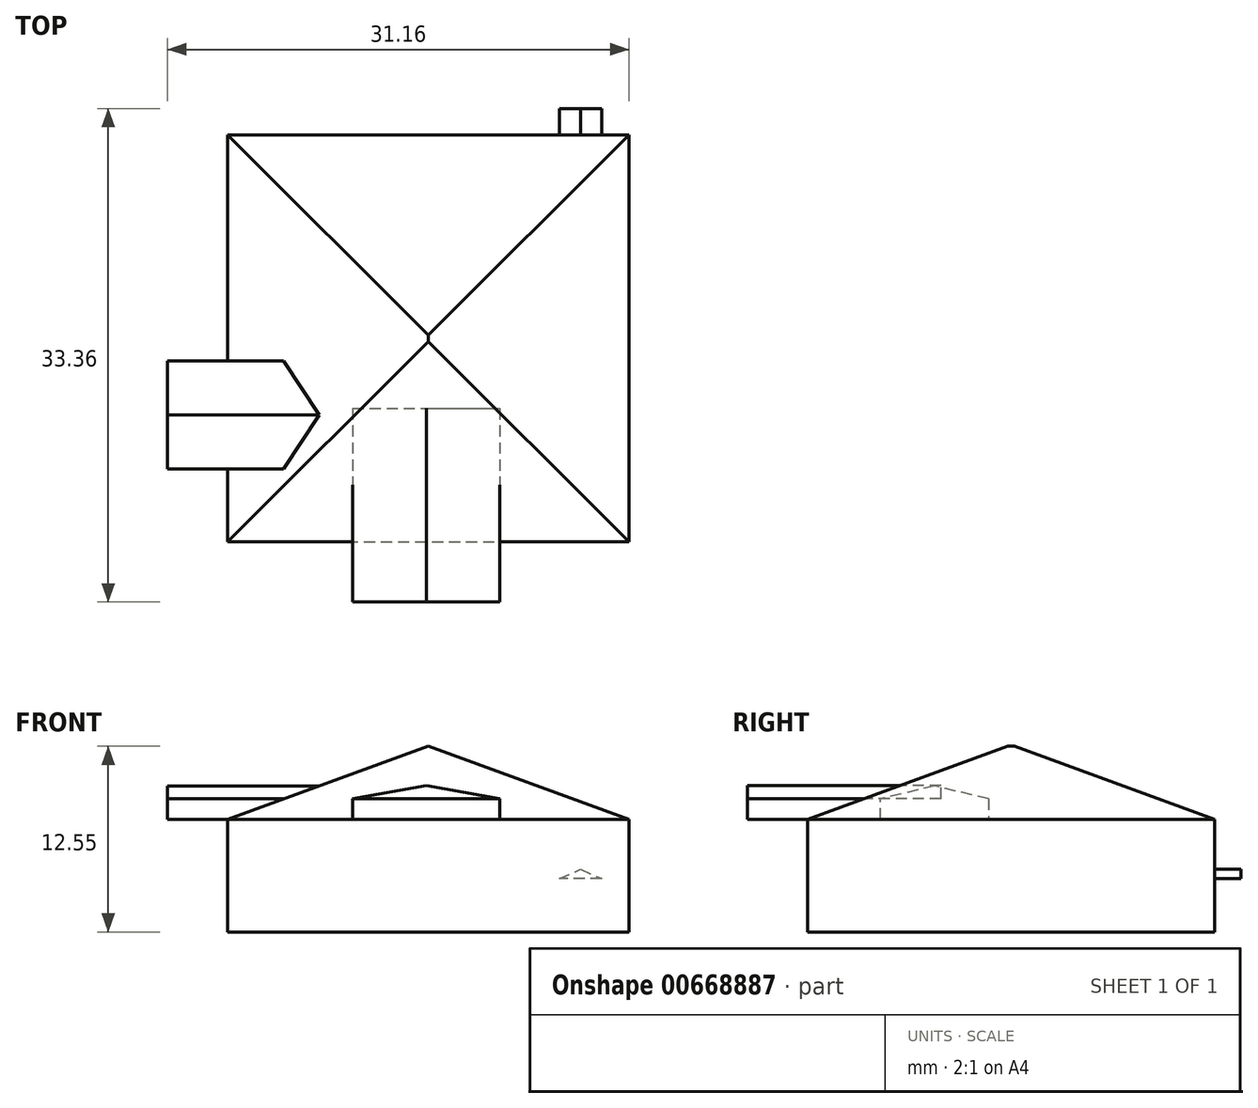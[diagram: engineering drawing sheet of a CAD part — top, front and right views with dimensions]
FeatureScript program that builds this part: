
annotation { "Feature Type Name" : "Feature", "Feature Type Description" : "" }
export const myFeature = defineFeature(function(context is Context, id is Id, definition is map)
    precondition{}
    {
        {
            var Q0;
            Q0=qCreatedBy(makeId("Top.planeOp"),FACE);
            var sketch = newSketch(context, id + "F0", { "sketchPlane" : qUnion([Q0])});
            skLineSegment(sketch, "E0.bottom", {"start": v(-13.65, 13.44) * mm, "end": v(13.44, 13.44) * mm});
            skLineSegment(sketch, "E0.top", {"start": v(-13.65, -14.08) * mm, "end": v(13.44, -14.08) * mm});
            skLineSegment(sketch, "E0.left", {"start": v(-13.65, 13.44) * mm, "end": v(-13.65, -14.08) * mm});
            skLineSegment(sketch, "E0.right", {"start": v(13.44, 13.44) * mm, "end": v(13.44, -14.08) * mm});
            skSolve(sketch);
        }
        {
            var Q0;
            Q0=makeQuery(id+"F0.imprint","IMPRINT",FACE,{"disambiguationData":[TD([[makeQuery(id+"F0.imprint","IMPRINT",EDGE,{"derivedFrom":sQuery(id+"F0.wireOp",EDGE,"E0.bottom")}),-1.0]])]});
            extrude(context, id + "F1", {"entities" : qUnion([Q0]), "depth" : 7.62 * mm, "offsetDistance" : 25.4 * mm});
        }
        {
            var Q0;
            Q0=makeQuery(id+"F1.opExtrude","CAP_FACE",FACE,{"disambiguationData":[OSD([sQuery(id+"F0.wireOp",EDGE,"E0.bottom"),sQuery(id+"F0.wireOp",EDGE,"E0.top"),sQuery(id+"F0.wireOp",EDGE,"E0.left"),sQuery(id+"F0.wireOp",EDGE,"E0.right")])],"isStart":false});
            var sketch = newSketch(context, id + "F2", { "sketchPlane" : qUnion([Q0])});
            skLineSegment(sketch, "E1", {"start": v(-13.65, 13.44) * mm, "end": v(-13.65, -14.08) * mm});
            skLineSegment(sketch, "E2", {"start": v(-13.65, -14.08) * mm, "end": v(13.44, -14.08) * mm});
            skLineSegment(sketch, "E3", {"start": v(13.44, -14.08) * mm, "end": v(13.44, 13.44) * mm});
            skLineSegment(sketch, "E4", {"start": v(13.44, 13.44) * mm, "end": v(-13.65, 13.44) * mm});
            skLineSegment(sketch, "E5", {"start": v(0, 0) * mm, "end": v(-13.65, 13.44) * mm});
            skLineSegment(sketch, "E6", {"start": v(0, 0) * mm, "end": v(13.44, 13.44) * mm});
            skLineSegment(sketch, "E7", {"start": v(0, 0) * mm, "end": v(13.44, -14.08) * mm});
            skLineSegment(sketch, "E8", {"start": v(0, 0) * mm, "end": v(-13.65, -14.08) * mm});
            skSolve(sketch);
        }
        {
            var Q0;
            Q0=makeQuery(id+"F2.imprint","IMPRINT",FACE,{"disambiguationData":[TD([[makeQuery(id+"F2.imprint","IMPRINT",EDGE,{"derivedFrom":sQuery(id+"F2.wireOp",EDGE,"E3")}),-1.0]])]});
            var Q1;
            Q1=makeQuery(id+"F2.imprint","IMPRINT",FACE,{"disambiguationData":[TD([[makeQuery(id+"F2.imprint","IMPRINT",EDGE,{"derivedFrom":sQuery(id+"F2.wireOp",EDGE,"E4")}),-1.0]])]});
            var Q2;
            Q2=makeQuery(id+"F2.imprint","IMPRINT",FACE,{"disambiguationData":[TD([[makeQuery(id+"F2.imprint","IMPRINT",EDGE,{"derivedFrom":sQuery(id+"F2.wireOp",EDGE,"E1")}),1.0]])]});
            var Q3;
            Q3=makeQuery(id+"F2.imprint","IMPRINT",FACE,{"disambiguationData":[TD([[makeQuery(id+"F2.imprint","IMPRINT",EDGE,{"derivedFrom":sQuery(id+"F2.wireOp",EDGE,"E2")}),1.0]])]});
            extrude(context, id + "F3", {"entities" : qUnion([Q0, Q1, Q2, Q3]), "operationType" : NewBodyOperationType.ADD, "depth" : 6.35 * mm, "offsetDistance" : 25.4 * mm, "hasDraft" : true, "draftAngle" : 70 * degree, "draftPullDirection" : true});
        }
        {
            var Q0;
            Q0=makeQuery(id+"F1.opExtrude","SWEPT_FACE",FACE,{"disambiguationData":[OSD([sQuery(id+"F0.wireOp",EDGE,"E0.top")])]});
            var sketch = newSketch(context, id + "F4", { "sketchPlane" : qUnion([Q0])});
            skLineSegment(sketch, "E9", {"start": v(4, 7.62) * mm, "end": v(-5.21, 7.62) * mm});
            skLineSegment(sketch, "E10", {"start": v(-5.21, 7.62) * mm, "end": v(-5.21, 9.02) * mm});
            skLineSegment(sketch, "E11", {"start": v(-5.21, 9.02) * mm, "end": v(3.68, 9.02) * mm});
            skLineSegment(sketch, "E12", {"start": v(3.68, 9.02) * mm, "end": v(4, 9.02) * mm});
            skLineSegment(sketch, "E13", {"start": v(4, 9.02) * mm, "end": v(4.73, 9.02) * mm});
            skLineSegment(sketch, "E14", {"start": v(4.73, 9.02) * mm, "end": v(4.73, 7.62) * mm});
            skLineSegment(sketch, "E15", {"start": v(4.73, 7.62) * mm, "end": v(4, 7.62) * mm});
            skSolve(sketch);
        }
        {
            var Q0;
            Q0 = qSketchRegion(id + "F4", true);
            var Q1;
            Q1=makeQuery(id+"F4.imprint","IMPRINT",FACE,{"disambiguationData":[TD([[makeQuery(id+"F4.imprint","IMPRINT",EDGE,{"derivedFrom":sQuery(id+"F4.wireOp",EDGE,"E10")}),-1.0]])]});
            extrude(context, id + "F5", {"entities" : qUnion([Q0, Q1]), "oppositeDirection" : true, "depth" : 5.84 * mm, "offsetDistance" : 25.4 * mm});
        }
        {
            var Q0;
            Q0=makeQuery(id+"F5.opExtrude","CAP_FACE",FACE,{"disambiguationData":[OSD([sQuery(id+"F4.wireOp",EDGE,"E10"),sQuery(id+"F4.wireOp",EDGE,"E11"),sQuery(id+"F4.wireOp",EDGE,"E12"),sQuery(id+"F4.wireOp",EDGE,"E9"),sQuery(id+"F4.wireOp",EDGE,"E13"),sQuery(id+"F4.wireOp",EDGE,"E14"),sQuery(id+"F4.wireOp",EDGE,"E15")])],"isStart":true});
            extrude(context, id + "F6", {"entities" : qUnion([Q0]), "operationType" : NewBodyOperationType.ADD, "depth" : 4.06 * mm, "offsetDistance" : 25.4 * mm});
        }
        {
            var Q0;
            Q0=makeQuery(id+"F6.opExtrude","CAP_FACE",FACE,{"disambiguationData":[OSD([sQuery(id+"F4.wireOp",EDGE,"E10"),sQuery(id+"F4.wireOp",EDGE,"E11"),sQuery(id+"F4.wireOp",EDGE,"E12"),sQuery(id+"F4.wireOp",EDGE,"E9"),sQuery(id+"F4.wireOp",EDGE,"E13"),sQuery(id+"F4.wireOp",EDGE,"E14"),sQuery(id+"F4.wireOp",EDGE,"E15")])],"isStart":false});
            var sketch = newSketch(context, id + "F7", { "sketchPlane" : qUnion([Q0])});
            skLineSegment(sketch, "E16", {"start": v(-5.21, 9.02) * mm, "end": v(-0.24, 9.89) * mm});
            skPoint(sketch, "E16.endSnap0", {"position": v(-0.24, 9.02) * mm});
            skLineSegment(sketch, "E17", {"start": v(-0.24, 9.89) * mm, "end": v(4.73, 9.02) * mm});
            skLineSegment(sketch, "E18", {"start": v(4.73, 9.02) * mm, "end": v(-5.21, 9.02) * mm});
            skSolve(sketch);
        }
        {
            var Q0;
            Q0=makeQuery(id+"F7.imprint","IMPRINT",FACE,{"disambiguationData":[TD([[makeQuery(id+"F7.imprint","IMPRINT",EDGE,{"derivedFrom":sQuery(id+"F7.wireOp",EDGE,"E16")}),-1.0]])]});
            extrude(context, id + "F8", {"entities" : qUnion([Q0]), "oppositeDirection" : true, "depth" : 13.08 * mm, "offsetDistance" : 25.4 * mm});
        }
        {
            var Q0;
            Q0=makeQuery(id+"F1.opExtrude","SWEPT_FACE",FACE,{"disambiguationData":[OSD([sQuery(id+"F0.wireOp",EDGE,"E0.left")])]});
            var sketch = newSketch(context, id + "F9", { "sketchPlane" : qUnion([Q0])});
            skLineSegment(sketch, "E19", {"start": v(1.93, 7.62) * mm, "end": v(9.16, 7.62) * mm});
            skLineSegment(sketch, "E20", {"start": v(9.16, 7.62) * mm, "end": v(9.16, 9) * mm});
            skLineSegment(sketch, "E21", {"start": v(9.16, 9) * mm, "end": v(1.83, 9) * mm});
            skLineSegment(sketch, "E22", {"start": v(1.83, 9) * mm, "end": v(1.83, 7.62) * mm});
            skLineSegment(sketch, "E23", {"start": v(1.83, 9) * mm, "end": v(5.5, 9.87) * mm});
            skPoint(sketch, "E23.endSnap0", {"position": v(5.5, 9) * mm});
            skLineSegment(sketch, "E24", {"start": v(5.5, 9.87) * mm, "end": v(9.16, 9) * mm});
            skSolve(sketch);
        }
        {
            var Q0;
            Q0 = qSketchRegion(id + "F9", true);
            var Q1;
            {var subQ1=sQuery(id+"F9.wireOp",EDGE,"E19");Q1=makeQuery(id+"F9.imprint","IMPRINT",FACE,{"disambiguationData":[TD([[makeQuery(id+"F9.imprint","IMPRINT",EDGE,{"derivedFrom":subQ1}),1.0]])]});}
            extrude(context, id + "F10", {"entities" : qUnion([Q0, Q1]), "operationType" : NewBodyOperationType.ADD, "oppositeDirection" : true, "depth" : 7.87 * mm, "offsetDistance" : 25.4 * mm});
        }
        {
            var Q0;
            {var subQ0=sQuery(id+"F0.wireOp",EDGE,"E0.left");Q0=makeQuery(id+"F10.boolean.opBoolean","MERGE",FACE,{"derivedFrom":[makeQuery(id+"F1.opExtrude","SWEPT_FACE",FACE,{"disambiguationData":[OSD([subQ0])]}),makeQuery(id+"F10.opExtrude","CAP_FACE",FACE,{"disambiguationData":[OSD([subQ0,sQuery(id+"F2.wireOp",EDGE,"E1"),sQuery(id+"F9.wireOp",EDGE,"E19"),sQuery(id+"F9.wireOp",EDGE,"E20"),sQuery(id+"F9.wireOp",EDGE,"E22"),sQuery(id+"F9.wireOp",EDGE,"E23"),sQuery(id+"F9.wireOp",EDGE,"E24")])],"isStart":true})]});}
            var sketch = newSketch(context, id + "F11", { "sketchPlane" : qUnion([Q0])});
            skLineSegment(sketch, "E25", {"start": v(1.83, 7.62) * mm, "end": v(9.16, 7.62) * mm});
            skLineSegment(sketch, "E26", {"start": v(9.16, 7.62) * mm, "end": v(9.16, 9) * mm});
            skLineSegment(sketch, "E27", {"start": v(9.16, 9) * mm, "end": v(5.5, 9.87) * mm});
            skLineSegment(sketch, "E28", {"start": v(5.5, 9.87) * mm, "end": v(1.83, 9) * mm});
            skLineSegment(sketch, "E29", {"start": v(1.83, 9) * mm, "end": v(1.83, 7.62) * mm});
            skSolve(sketch);
        }
        {
            var Q0;
            Q0 = qSketchRegion(id + "F11", true);
            extrude(context, id + "F12", {"entities" : qUnion([Q0]), "operationType" : NewBodyOperationType.ADD, "depth" : 4.06 * mm, "offsetDistance" : 25.4 * mm});
        }
        {
            var Q0;
            Q0=makeQuery(id+"F1.opExtrude","SWEPT_FACE",FACE,{"disambiguationData":[OSD([sQuery(id+"F0.wireOp",EDGE,"E0.bottom")])]});
            var sketch = newSketch(context, id + "F13", { "sketchPlane" : qUnion([Q0])});
            skLineSegment(sketch, "E30", {"start": v(-11.61, 3.6) * mm, "end": v(-8.75, 3.6) * mm});
            skLineSegment(sketch, "E31", {"start": v(-8.75, 3.6) * mm, "end": v(-10.18, 4.24) * mm});
            skPoint(sketch, "E31.endSnap0", {"position": v(-10.18, 3.6) * mm});
            skLineSegment(sketch, "E32", {"start": v(-10.18, 4.24) * mm, "end": v(-11.61, 3.6) * mm});
            skSolve(sketch);
        }
        {
            var Q0;
            Q0 = qSketchRegion(id + "F13", true);
            extrude(context, id + "F14", {"entities" : qUnion([Q0]), "operationType" : NewBodyOperationType.ADD, "depth" : 1.78 * mm, "offsetDistance" : 25.4 * mm});
        }
    });
